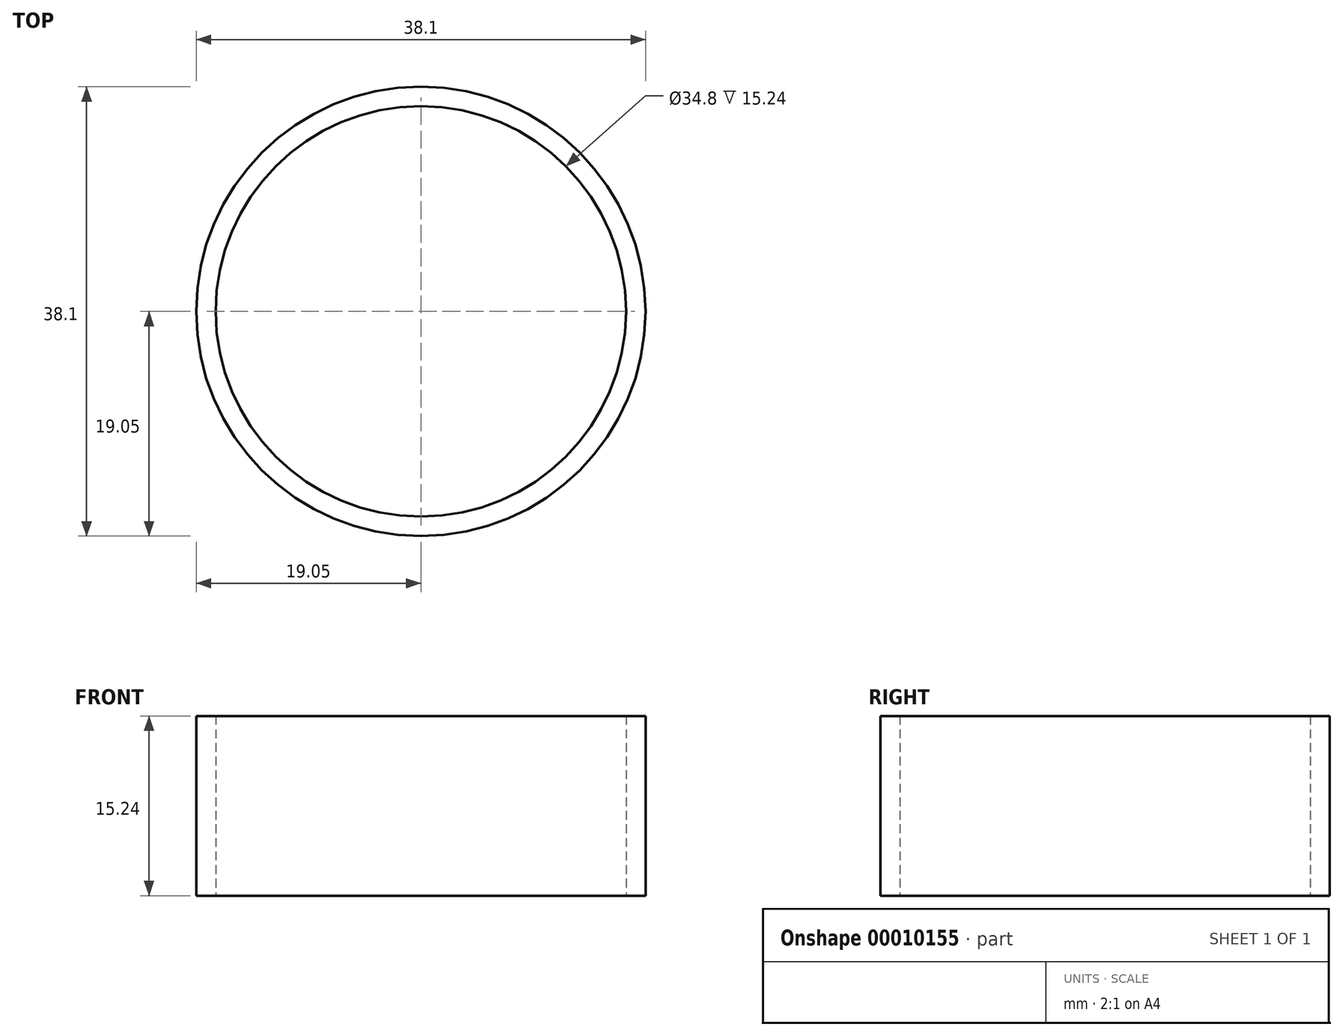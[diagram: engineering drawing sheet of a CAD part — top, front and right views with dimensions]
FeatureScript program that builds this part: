
annotation { "Feature Type Name" : "Feature", "Feature Type Description" : "" }
export const myFeature = defineFeature(function(context is Context, id is Id, definition is map)
    precondition{}
    {
        {
            var Q0;
            Q0=qCreatedBy(makeId("Top.planeOp"),FACE);
            var sketch = newSketch(context, id + "F0", { "sketchPlane" : qUnion([Q0])});
            skCircle(sketch, "E0", {"center": v(0, 0) * mm, "radius": 19.05 * mm});
            skCircle(sketch, "E1", {"center": v(0, 0) * mm, "radius": 17.4 * mm});
            skSolve(sketch);
        }
        {
            var Q0;
            Q0 = qSketchRegion(id + "F0", true);
            extrude(context, id + "F1", {"entities" : qUnion([Q0]), "depth" : 15.24 * mm});
        }
    });
